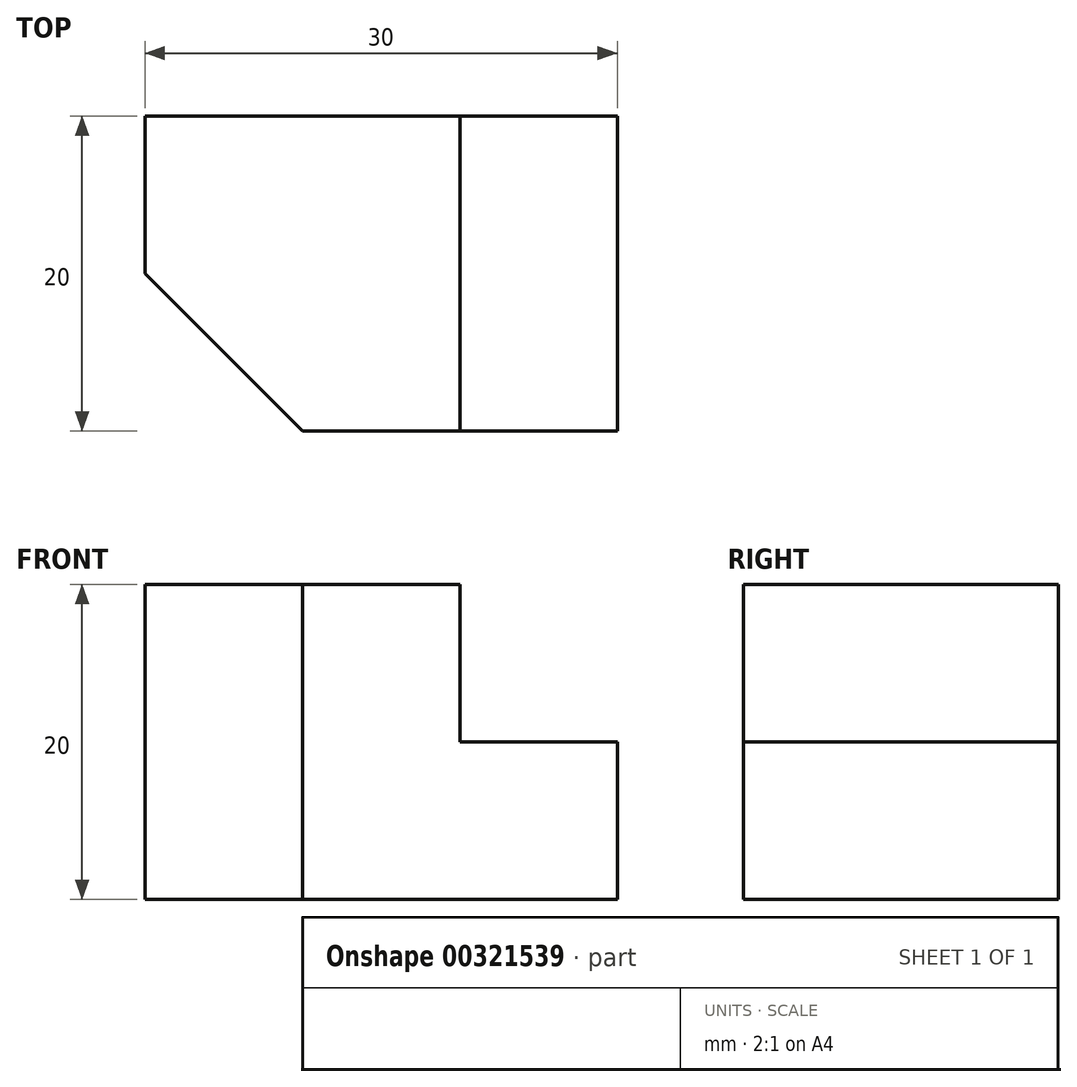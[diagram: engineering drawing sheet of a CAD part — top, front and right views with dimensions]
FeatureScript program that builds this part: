
annotation { "Feature Type Name" : "Feature", "Feature Type Description" : "" }
export const myFeature = defineFeature(function(context is Context, id is Id, definition is map)
    precondition{}
    {
        {
            var Q0;
            Q0=qCreatedBy(makeId("Front.planeOp"),FACE);
            var sketch = newSketch(context, id + "F0", { "sketchPlane" : qUnion([Q0])});
            skLineSegment(sketch, "E0", {"start": v(0, 0) * mm, "end": v(0, 20) * mm});
            skLineSegment(sketch, "E1", {"start": v(0, 20) * mm, "end": v(10, 20) * mm});
            skLineSegment(sketch, "E2", {"start": v(10, 20) * mm, "end": v(10, 10) * mm});
            skLineSegment(sketch, "E3", {"start": v(10, 10) * mm, "end": v(20, 10) * mm});
            skLineSegment(sketch, "E4", {"start": v(20, 10) * mm, "end": v(20, 0) * mm});
            skLineSegment(sketch, "E5", {"start": v(20, 0) * mm, "end": v(0, 0) * mm});
            skSolve(sketch);
        }
        {
            var Q0;
            Q0=makeQuery(id+"F0.imprint","IMPRINT",FACE,{"disambiguationData":[TD([[makeQuery(id+"F0.imprint","IMPRINT",EDGE,{"derivedFrom":sQuery(id+"F0.wireOp",EDGE,"E0")}),-1.0]])]});
            extrude(context, id + "F1", {"entities" : qUnion([Q0]), "depth" : 20 * mm});
        }
        {
            var Q0;
            Q0=makeQuery(id+"F1.opExtrude","SWEPT_FACE",FACE,{"disambiguationData":[OSD([sQuery(id+"F0.wireOp",EDGE,"E5")])]});
            var sketch = newSketch(context, id + "F2", { "sketchPlane" : qUnion([Q0])});
            skLineSegment(sketch, "E6", {"start": v(0, 0) * mm, "end": v(-10, 0) * mm});
            skLineSegment(sketch, "E7", {"start": v(-10, 0) * mm, "end": v(-10, 10) * mm});
            skLineSegment(sketch, "E8", {"start": v(-10, 10) * mm, "end": v(0, 20) * mm});
            skLineSegment(sketch, "E9", {"start": v(0, 20) * mm, "end": v(0, 0) * mm});
            skSolve(sketch);
        }
        {
            var Q0;
            Q0=makeQuery(id+"F2.imprint","IMPRINT",FACE,{"disambiguationData":[TD([[makeQuery(id+"F2.imprint","IMPRINT",EDGE,{"derivedFrom":sQuery(id+"F2.wireOp",EDGE,"E6")}),-1.0]])]});
            extrude(context, id + "F3", {"entities" : qUnion([Q0]), "operationType" : NewBodyOperationType.ADD, "oppositeDirection" : true, "depth" : 20 * mm});
        }
    });
